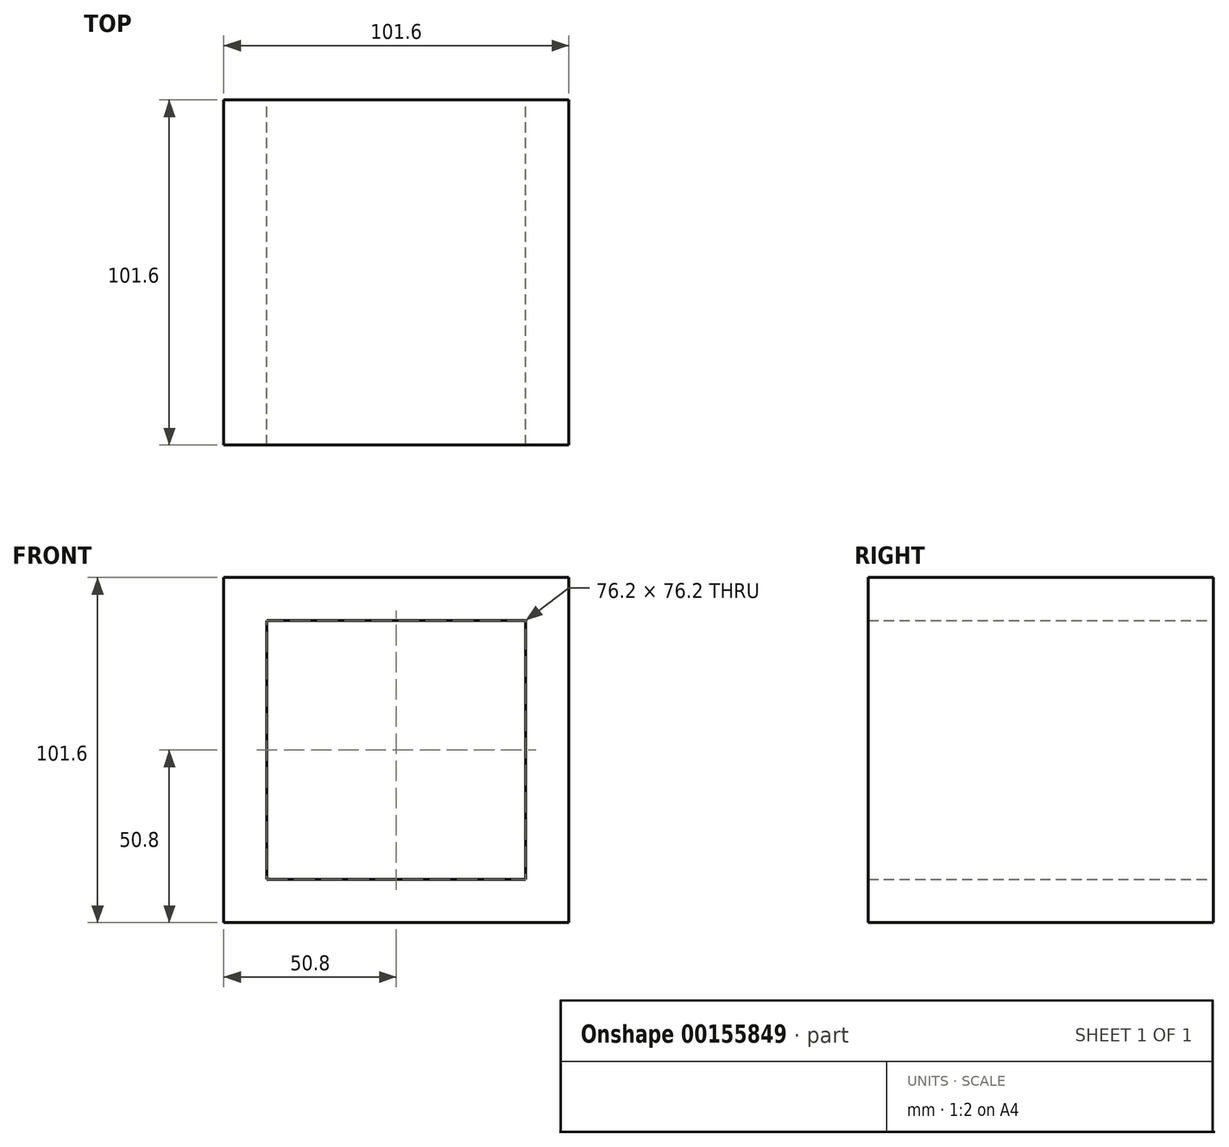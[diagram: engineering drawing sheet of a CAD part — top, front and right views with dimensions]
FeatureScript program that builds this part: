
annotation { "Feature Type Name" : "Feature", "Feature Type Description" : "" }
export const myFeature = defineFeature(function(context is Context, id is Id, definition is map)
    precondition{}
    {
        {
            var Q0;
            Q0=qCreatedBy(makeId("Front.planeOp"),FACE);
            var sketch = newSketch(context, id + "F0", { "sketchPlane" : qUnion([Q0])});
            skLineSegment(sketch, "E0.bottom", {"start": v(-50.8, 50.8) * mm, "end": v(50.8, 50.8) * mm});
            skLineSegment(sketch, "E0.top", {"start": v(-50.8, -50.8) * mm, "end": v(50.8, -50.8) * mm});
            skLineSegment(sketch, "E0.left", {"start": v(-50.8, 50.8) * mm, "end": v(-50.8, -50.8) * mm});
            skLineSegment(sketch, "E0.right", {"start": v(50.8, 50.8) * mm, "end": v(50.8, -50.8) * mm});
            skPoint(sketch, "E0.middle", {"position": v(0, 0) * mm});
            skLineSegment(sketch, "E1.bottom", {"start": v(38.1, -38.1) * mm, "end": v(-38.1, -38.1) * mm});
            skLineSegment(sketch, "E1.top", {"start": v(38.1, 38.1) * mm, "end": v(-38.1, 38.1) * mm});
            skLineSegment(sketch, "E1.left", {"start": v(38.1, -38.1) * mm, "end": v(38.1, 38.1) * mm});
            skLineSegment(sketch, "E1.right", {"start": v(-38.1, -38.1) * mm, "end": v(-38.1, 38.1) * mm});
            skSolve(sketch);
        }
        {
            var Q0;
            Q0=makeQuery(id+"F0.imprint","IMPRINT",FACE,{"disambiguationData":[TD([[makeQuery(id+"F0.imprint","IMPRINT",EDGE,{"derivedFrom":sQuery(id+"F0.wireOp",EDGE,"E0.bottom")}),-1.0]])]});
            extrude(context, id + "F1", {"entities" : qUnion([Q0]), "depth" : 101.6 * mm});
        }
    });
